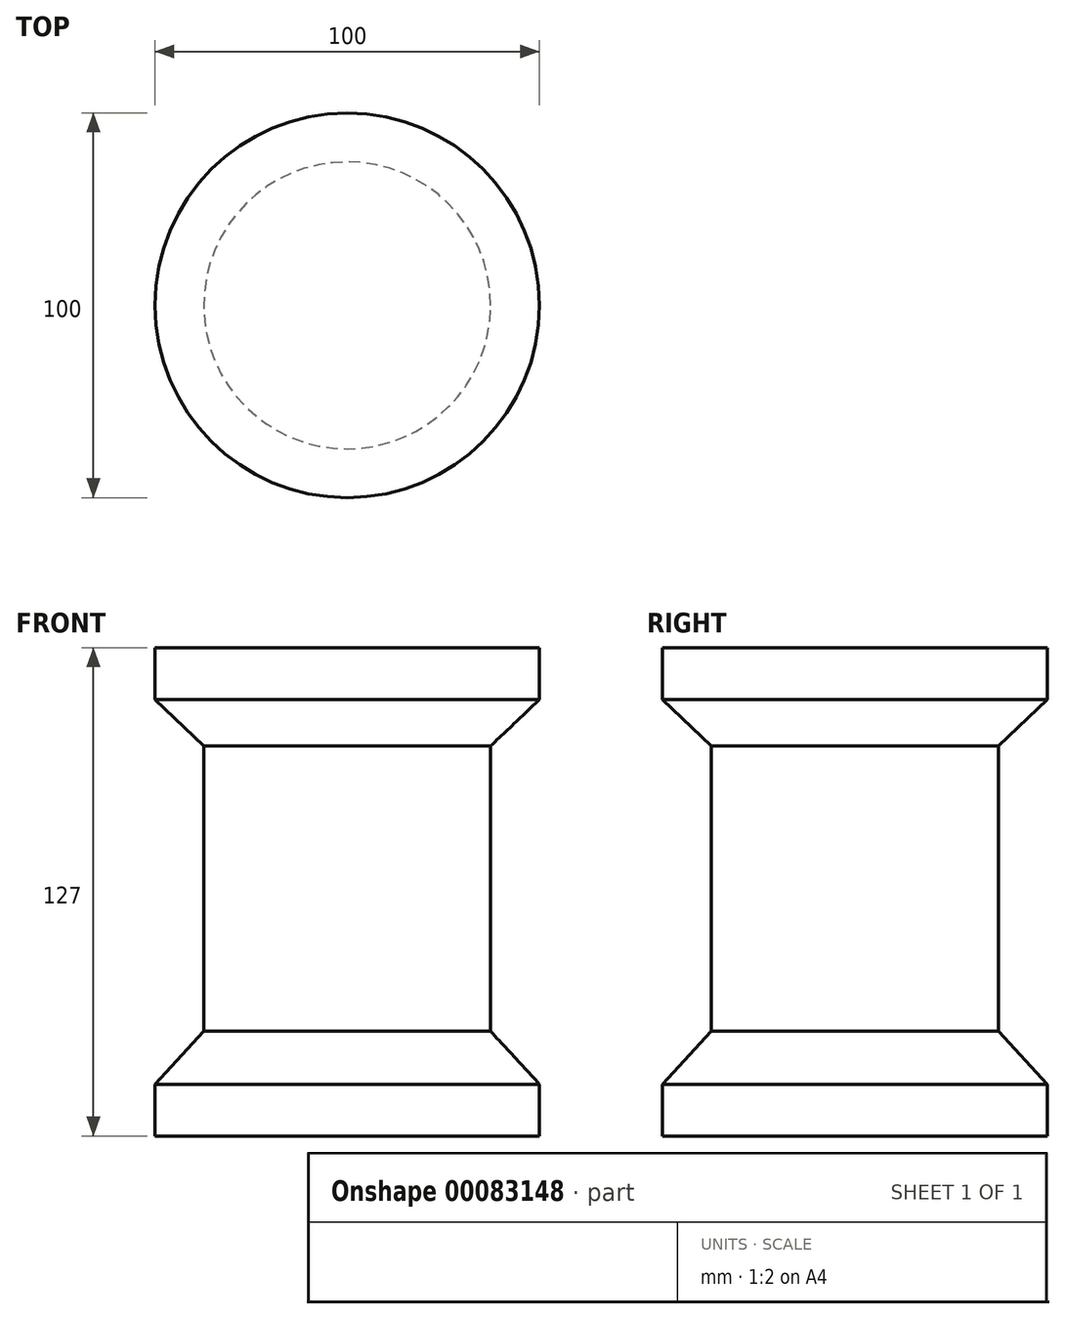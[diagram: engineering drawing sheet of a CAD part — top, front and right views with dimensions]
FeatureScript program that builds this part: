
annotation { "Feature Type Name" : "Feature", "Feature Type Description" : "" }
export const myFeature = defineFeature(function(context is Context, id is Id, definition is map)
    precondition{}
    {
        {
            var Q0;
            Q0=qCreatedBy(makeId("Top.planeOp"),FACE);
            var sketch = newSketch(context, id + "F0", { "sketchPlane" : qUnion([Q0])});
            skCircle(sketch, "E0", {"center": v(0, 0) * mm, "radius": 50 * mm});
            skSolve(sketch);
        }
        {
            var Q0;
            Q0=makeQuery(id+"F0.imprint","IMPRINT",FACE,{"disambiguationData":[TD([[makeQuery(id+"F0.imprint","IMPRINT",EDGE,{"derivedFrom":sQuery(id+"F0.wireOp",EDGE,"E0")}),1.0]])]});
            extrude(context, id + "F1", {"entities" : qUnion([Q0]), "depth" : 127 * mm});
        }
        {
            var Q0;
            Q0=qCreatedBy(makeId("Front.planeOp"),FACE);
            var sketch = newSketch(context, id + "F2", { "sketchPlane" : qUnion([Q0])});
            skLineSegment(sketch, "E1", {"start": v(0, 0) * mm, "end": v(0, 123.3) * mm, "construction": true});
            skLineSegment(sketch, "E2", {"start": v(-50, 127) * mm, "end": v(-50, 113.53) * mm});
            skLineSegment(sketch, "E3", {"start": v(-50, 113.53) * mm, "end": v(-37.3, 101.44) * mm});
            skLineSegment(sketch, "E4", {"start": v(-37.3, 101.44) * mm, "end": v(-37.3, 27.2) * mm});
            skLineSegment(sketch, "E5", {"start": v(-37.3, 27.2) * mm, "end": v(-50, 13.47) * mm});
            skLineSegment(sketch, "E6", {"start": v(-50, 13.47) * mm, "end": v(-50, 0) * mm});
            skLineSegment(sketch, "E7", {"start": v(-50, 0) * mm, "end": v(-84.93, 0) * mm});
            skLineSegment(sketch, "E8", {"start": v(-84.93, 0) * mm, "end": v(-84.93, 127) * mm});
            skLineSegment(sketch, "E9", {"start": v(-84.93, 127) * mm, "end": v(-50, 127) * mm});
            skSolve(sketch);
        }
        {
            var Q0;
            Q0=makeQuery(id+"F2.imprint","IMPRINT",FACE,{"disambiguationData":[TD([[makeQuery(id+"F2.imprint","IMPRINT",EDGE,{"derivedFrom":sQuery(id+"F2.wireOp",EDGE,"E2")}),-1.0]])]});
            var Q1;
            Q1=sQuery(id+"F2.wireOp",EDGE,"E1");
            revolve(context, id + "F3", {"operationType" : NewBodyOperationType.REMOVE, "entities" : qUnion([Q0]), "axis" : qUnion([Q1]), "revolveType" : RevolveType.FULL, "oppositeDirection" : true});
        }
    });
